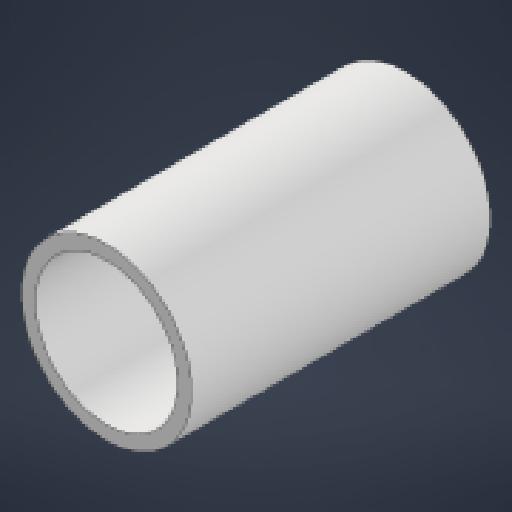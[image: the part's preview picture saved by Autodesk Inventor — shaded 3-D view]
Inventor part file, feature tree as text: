
AUTODESK INVENTOR PART (.ipt)
format: ipt  version: 2024.1 (Build 281209000, 209)  size: 137,728 bytes
history: native  units: in
note: dims shown in document units (in); Inventor stores cm internally (conversion verified against a paired STEP export)
features: other x4, reference x2, extrude x1, sketch x1
ambient origin geometry x8: Origin, YZ Plane, XZ Plane, XY Plane, X Axis, Y Axis, Z Axis, Center Point
bodies: Solid1 (feature_tree)
feature tree (8):
  extrude  "Extrusion1"  Depth=0.273in
  sketch  "Sketch1"  dims[d0=0.002in d1=0.005in d2=0.273in d3=0.0in]
  reference  "Reference1"
  reference  "Reference2"
  other  "<userpath>\Documents\School\FallCAD\Bio\Bio.iam"
  other  "Bio.iam"
  other  "Servo HS425BB:1"
  other  "ServoMount:1"
